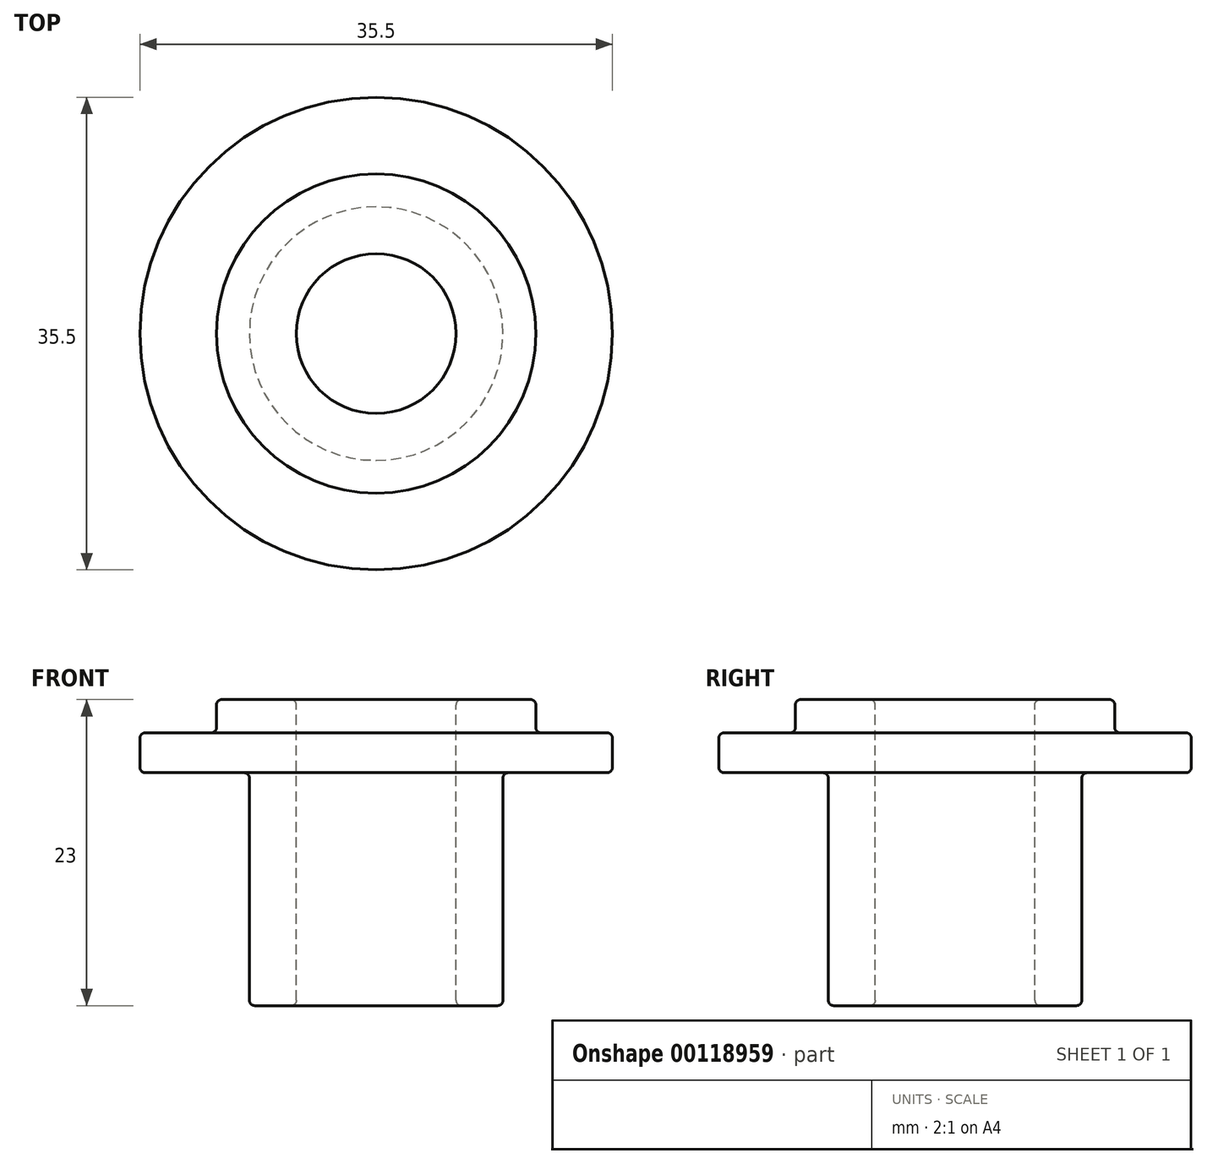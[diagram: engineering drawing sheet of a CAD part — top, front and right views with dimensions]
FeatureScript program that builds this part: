
annotation { "Feature Type Name" : "Feature", "Feature Type Description" : "" }
export const myFeature = defineFeature(function(context is Context, id is Id, definition is map)
    precondition{}
    {
        {
            var Q0;
            Q0=qCreatedBy(makeId("Top.planeOp"),FACE);
            var sketch = newSketch(context, id + "F0", { "sketchPlane" : qUnion([Q0])});
            skCircle(sketch, "E0", {"center": v(0, 0) * mm, "radius": 9.53 * mm});
            skCircle(sketch, "E1", {"center": v(0, 0) * mm, "radius": 6 * mm});
            skSolve(sketch);
        }
        {
            var Q0;
            Q0=qSketchRegion(id+"F0",true);
            extrude(context, id + "F1", {"entities" : qUnion([Q0]), "oppositeDirection" : true, "depth" : 17.5 * mm});
        }
        {
            var Q0;
            Q0=qCreatedBy(makeId("Top.planeOp"),FACE);
            var sketch = newSketch(context, id + "F2", { "sketchPlane" : qUnion([Q0])});
            skCircle(sketch, "E2", {"center": v(0, 0) * mm, "radius": 17.75 * mm});
            skCircle(sketch, "E3.0", {"center": v(0, 0) * mm, "radius": 6 * mm});
            skSolve(sketch);
        }
        {
            var Q0;
            Q0=qSketchRegion(id+"F2",true);
            extrude(context, id + "F3", {"entities" : qUnion([Q0]), "operationType" : NewBodyOperationType.ADD, "depth" : 3 * mm});
        }
        {
            var Q0;
            Q0=makeQuery(id+"F3.opExtrude","CAP_FACE",FACE,{"disambiguationData":[OSD([sQuery(id+"F2.wireOp",EDGE,"E2"),sQuery(id+"F2.wireOp",EDGE,"E3.0")])],"isStart":false});
            var sketch = newSketch(context, id + "F4", { "sketchPlane" : qUnion([Q0])});
            skCircle(sketch, "E4.0", {"center": v(0, 0) * mm, "radius": 6 * mm});
            skCircle(sketch, "E5", {"center": v(0, 0) * mm, "radius": 12 * mm});
            skSolve(sketch);
        }
        {
            var Q0;
            Q0=qSketchRegion(id+"F4",true);
            extrude(context, id + "F5", {"entities" : qUnion([Q0]), "operationType" : NewBodyOperationType.ADD, "depth" : 2.5 * mm});
        }
        {
            var Q0;
            Q0=makeQuery(id+"F5.opExtrude","CAP_FACE",FACE,{"disambiguationData":[OSD([sQuery(id+"F4.wireOp",EDGE,"E4.0"),sQuery(id+"F4.wireOp",EDGE,"E5")])],"isStart":false});
            var Q1;
            Q1=makeQuery(id+"F3.opExtrude","CAP_FACE",FACE,{"disambiguationData":[OSD([sQuery(id+"F2.wireOp",EDGE,"E2"),sQuery(id+"F2.wireOp",EDGE,"E3.0")])],"isStart":false});
            var Q2;
            Q2=makeQuery(id+"F3.opExtrude","CAP_FACE",FACE,{"disambiguationData":[OSD([sQuery(id+"F2.wireOp",EDGE,"E2"),sQuery(id+"F2.wireOp",EDGE,"E3.0")])],"isStart":true});
            var Q3;
            Q3=makeQuery(id+"F1.opExtrude","CAP_FACE",FACE,{"disambiguationData":[OSD([sQuery(id+"F0.wireOp",EDGE,"E0"),sQuery(id+"F0.wireOp",EDGE,"E1")])],"isStart":false});
            fillet(context, id + "F6", {"entities" : qUnion([Q0, Q1, Q2, Q3]), "radius" : 0.4 * mm, "tangentPropagation" : true, "allowEdgeOverflow" : false});
        }
    });
